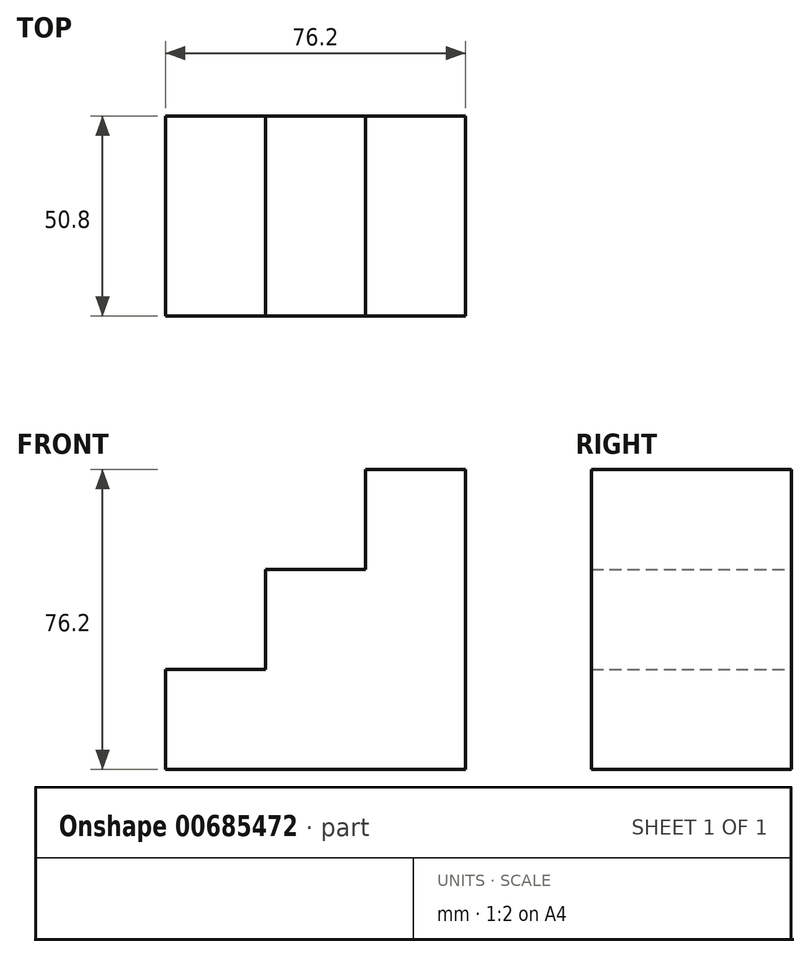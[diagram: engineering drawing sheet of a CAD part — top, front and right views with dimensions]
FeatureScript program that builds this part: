
annotation { "Feature Type Name" : "Feature", "Feature Type Description" : "" }
export const myFeature = defineFeature(function(context is Context, id is Id, definition is map)
    precondition{}
    {
        {
            var Q0;
            Q0=qCreatedBy(makeId("Front.planeOp"),FACE);
            var sketch = newSketch(context, id + "F0", { "sketchPlane" : qUnion([Q0])});
            skLineSegment(sketch, "E0", {"start": v(-47.83, -45.35) * mm, "end": v(28.37, -45.35) * mm});
            skLineSegment(sketch, "E1", {"start": v(28.37, -45.35) * mm, "end": v(28.37, 30.85) * mm});
            skLineSegment(sketch, "E2", {"start": v(28.37, 30.85) * mm, "end": v(2.97, 30.85) * mm});
            skLineSegment(sketch, "E3", {"start": v(2.97, 30.85) * mm, "end": v(2.97, 5.45) * mm});
            skLineSegment(sketch, "E4", {"start": v(2.97, 5.45) * mm, "end": v(-22.43, 5.45) * mm});
            skLineSegment(sketch, "E5", {"start": v(-22.43, 5.45) * mm, "end": v(-22.43, -19.95) * mm});
            skLineSegment(sketch, "E6", {"start": v(-22.43, -19.95) * mm, "end": v(-47.83, -19.95) * mm});
            skLineSegment(sketch, "E7", {"start": v(-47.83, -19.95) * mm, "end": v(-47.83, -45.35) * mm});
            skSolve(sketch);
        }
        {
            var Q0;
            Q0=makeQuery(id+"F0.imprint","IMPRINT",FACE,{"disambiguationData":[TD([[makeQuery(id+"F0.imprint","IMPRINT",EDGE,{"derivedFrom":sQuery(id+"F0.wireOp",EDGE,"E0")}),1.0]])]});
            extrude(context, id + "F1", {"entities" : qUnion([Q0]), "depth" : 50.8 * mm, "offsetDistance" : 25.4 * mm});
        }
    });
